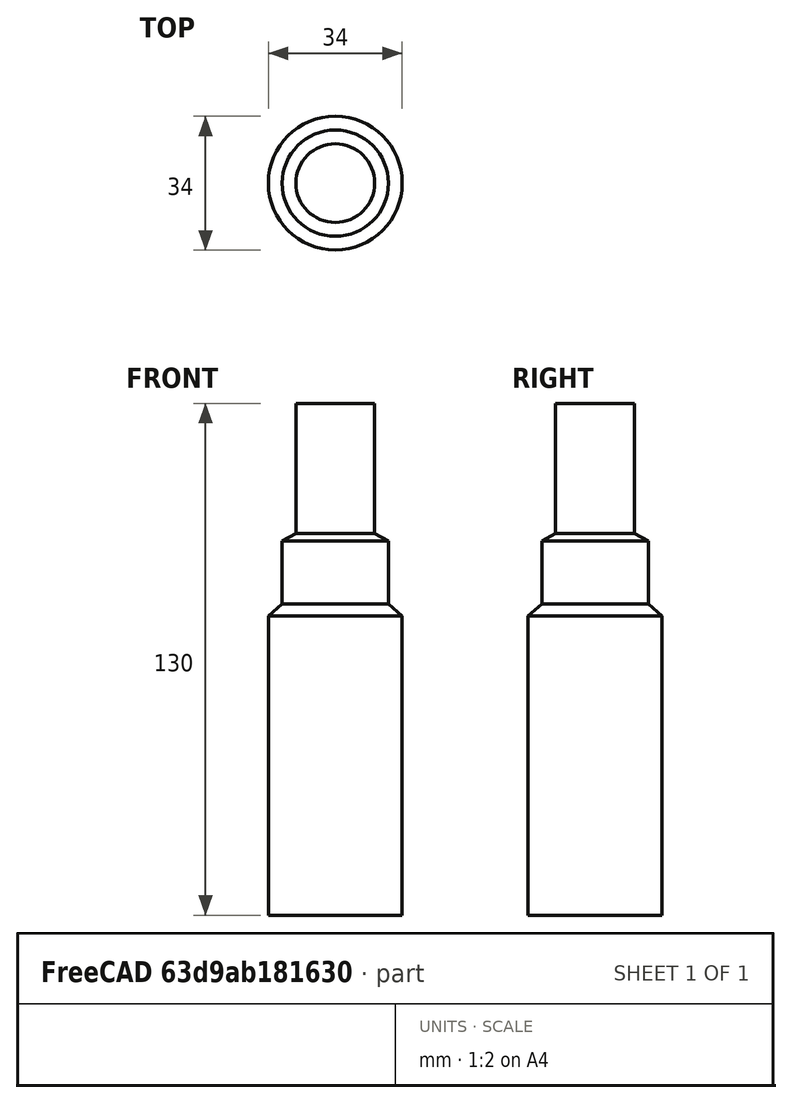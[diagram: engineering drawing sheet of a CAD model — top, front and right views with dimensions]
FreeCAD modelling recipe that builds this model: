
FCSTD DOCUMENT  (FreeCAD 0.19R24291 (Git))
Label: cleanerBottle
License: All rights reserved
LicenseURL: http://en.wikipedia.org/wiki/All_rights_reserved
objects: Sketcher::SketchObject×1, PartDesign::Revolution×1, PartDesign::Body×1
note: 4 computed .brp shape members not serialized (recipe doc carries the construction recipe); baked Part::Feature solids carry a one-line shape summary decoded from their .brp

FEATURE [Sketcher::SketchObject] Sketch
  FullyConstrained = true
  MapMode = 5
  Placement = pos=(0,0,0) rot=(1,0,0;1.5708rad)
  Support = -> [XZ_Plane]
  expr: Constraints[17] = 20 / 2
  expr: Constraints[16] = 27 / 2
  expr: Constraints[15] = 34 / 2
  sketch-geometry (8):
    g0: LineSegment StartX=0 StartY=0 StartZ=0 EndX=-17 EndY=0 EndZ=0
    g1: LineSegment StartX=-17 StartY=0 StartZ=0 EndX=-17 EndY=76 EndZ=0
    g2: LineSegment StartX=-17 StartY=76 StartZ=0 EndX=-13.5 EndY=79.08 EndZ=0
    g3: LineSegment StartX=-13.5 StartY=79.08 StartZ=0 EndX=-13.5 EndY=95.08 EndZ=0
    g4: LineSegment StartX=-13.5 StartY=95.08 StartZ=0 EndX=-10 EndY=97 EndZ=0
    g5: LineSegment StartX=-10 StartY=97 StartZ=0 EndX=-10 EndY=130 EndZ=0
    g6: LineSegment StartX=-10 StartY=130 StartZ=0 EndX=0 EndY=130 EndZ=0
    g7: LineSegment StartX=0 StartY=130 StartZ=0 EndX=0 EndY=0 EndZ=0
  constraints (23):
    c: Coincident(g-1,g0)
    c: PointOnObject(g0,g-1)
    c: Coincident(g0,g1)
    c: Vertical(g1)
    c: Coincident(g1,g2)
    c: Coincident(g2,g3)
    c: Vertical(g3)
    c: Coincident(g3,g4)
    c: Coincident(g4,g5)
    c: Vertical(g5)
    c: Coincident(g5,g6)
    c: PointOnObject(g6,g-2)
    c: Horizontal(g6)
    c: Coincident(g6,g7)
    c: Coincident(g7,g0)
    c: DistanceX(g0,g0) = 17
    c: DistanceX(g2,g0) = 13.5
    c: DistanceX(g4,g0) = 10
    c: DistanceY(g0,g1) = 76
    c: DistanceY(g0,g6) = 130
    c: DistanceY(g4,g5) = 33
    c: DistanceY(g2,g3) = 16
    c: DistanceY(g3,g4) = 1.92
FEATURE [PartDesign::Revolution] Revolution
  Angle = 360
  Axis = (0,2e-16,1)
  Base = (0,0,0)
  Placement = pos=(0,0,0) rot=(1,0,0;1.5708rad)
  Profile = -> Sketch
  ReferenceAxis = -> Sketch [V_Axis]
FEATURE [PartDesign::Body] Body
  Group = -> [Sketch,Revolution]
  Origin = -> Origin
  Tip = -> Revolution
